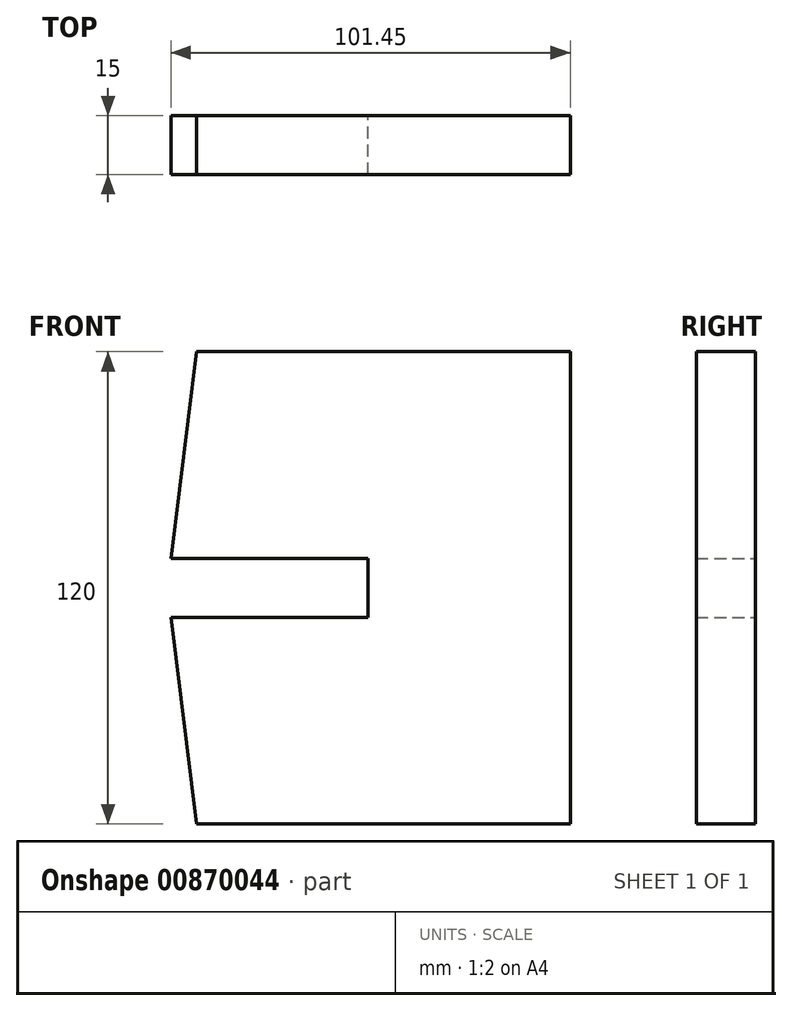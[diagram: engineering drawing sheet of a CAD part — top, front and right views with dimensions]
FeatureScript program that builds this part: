
annotation { "Feature Type Name" : "Feature", "Feature Type Description" : "" }
export const myFeature = defineFeature(function(context is Context, id is Id, definition is map)
    precondition{}
    {
        {
            var Q0;
            Q0=qCreatedBy(makeId("Front.planeOp"),FACE);
            var sketch = newSketch(context, id + "F0", { "sketchPlane" : qUnion([Q0])});
            skLineSegment(sketch, "E0", {"start": v(-95, 52.5) * mm, "end": v(0, 52.5) * mm});
            skLineSegment(sketch, "E1", {"start": v(0, 52.5) * mm, "end": v(0, -67.5) * mm});
            skLineSegment(sketch, "E2", {"start": v(0, -67.5) * mm, "end": v(-95, -67.5) * mm});
            skLineSegment(sketch, "E3", {"start": v(-95, -67.5) * mm, "end": v(-101.45, -15) * mm});
            skLineSegment(sketch, "E4", {"start": v(-101.45, -15) * mm, "end": v(-51.45, -15) * mm});
            skLineSegment(sketch, "E5", {"start": v(-51.45, -15) * mm, "end": v(-51.45, 0) * mm});
            skLineSegment(sketch, "E6", {"start": v(-51.45, 0) * mm, "end": v(-101.45, 0) * mm});
            skLineSegment(sketch, "E7", {"start": v(-101.45, 0) * mm, "end": v(-95, 52.5) * mm});
            skLineSegment(sketch, "E8", {"start": v(-101.45, 0) * mm, "end": v(-101.45, -15) * mm, "construction": true});
            skSolve(sketch);
        }
        {
            var Q0;
            Q0 = qSketchRegion(id + "F0", true);
            extrude(context, id + "F1", {"entities" : qUnion([Q0]), "depth" : 15 * mm, "offsetDistance" : 25 * mm});
        }
    });
